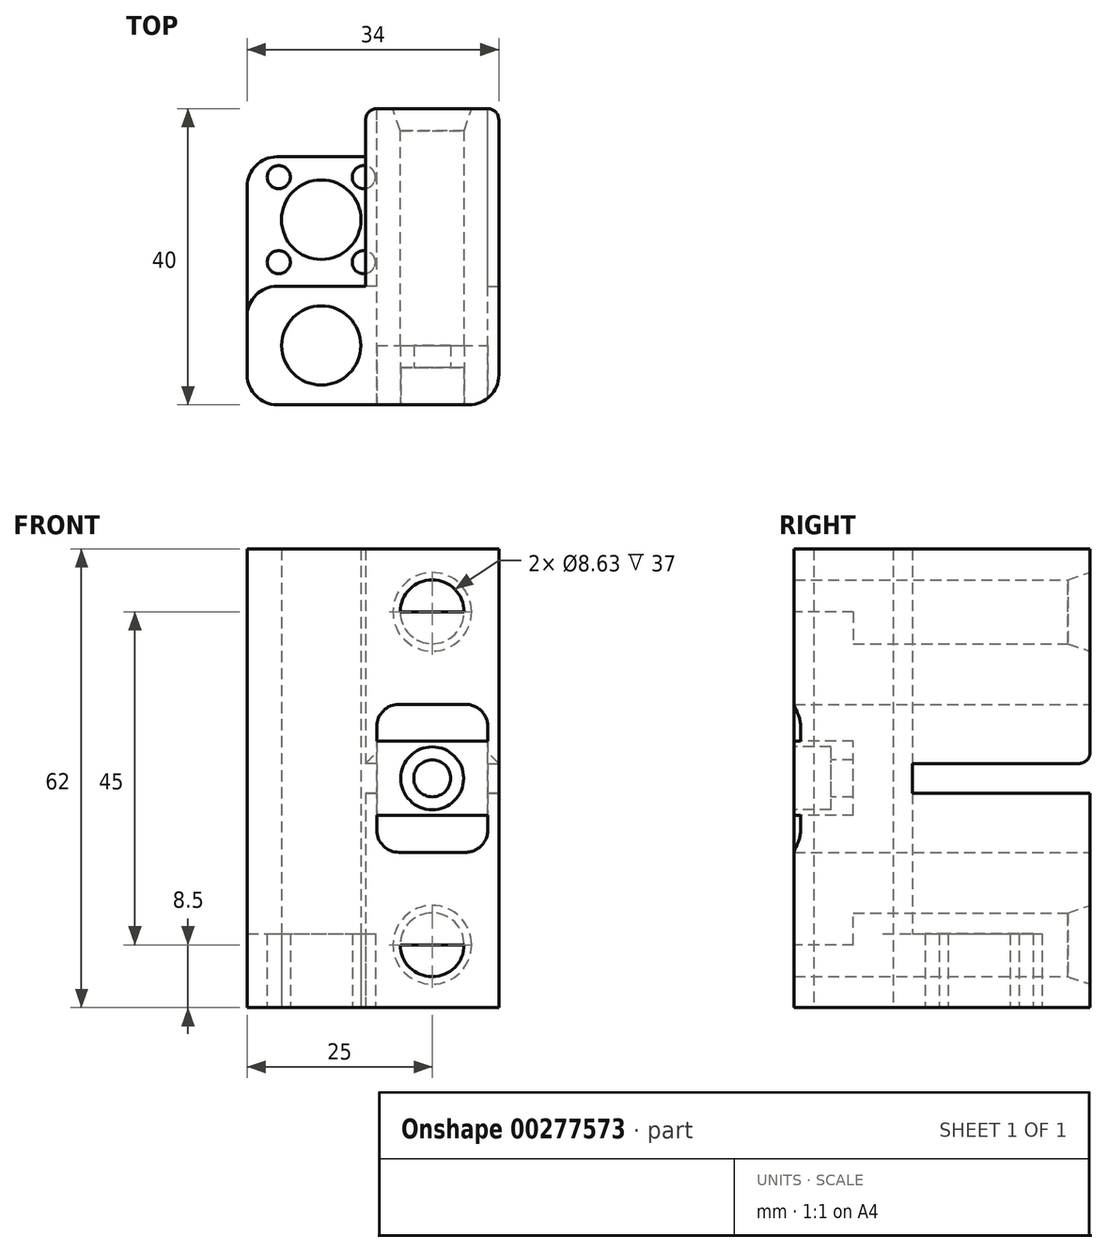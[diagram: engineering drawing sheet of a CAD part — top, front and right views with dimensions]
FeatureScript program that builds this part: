
annotation { "Feature Type Name" : "Feature", "Feature Type Description" : "" }
export const myFeature = defineFeature(function(context is Context, id is Id, definition is map)
    precondition{}
    {
        {
            var Q0;
            Q0=qCreatedBy(makeId("Front.planeOp"),FACE);
            var sketch = newSketch(context, id + "F0", { "sketchPlane" : qUnion([Q0])});
            skLineSegment(sketch, "E0.bottom", {"start": v(9, 31) * mm, "end": v(-9, 31) * mm});
            skLineSegment(sketch, "E0.top", {"start": v(9, -31) * mm, "end": v(-9, -31) * mm});
            skLineSegment(sketch, "E0.left", {"start": v(9, 31) * mm, "end": v(9, -31) * mm});
            skLineSegment(sketch, "E0.right", {"start": v(-9, 31) * mm, "end": v(-9, -31) * mm});
            skPoint(sketch, "E0.middle", {"position": v(0, 0) * mm});
            skCircle(sketch, "E1", {"center": v(0, 22.5) * mm, "radius": 4.32 * mm});
            skCircle(sketch, "E2", {"center": v(0, -22.5) * mm, "radius": 4.32 * mm});
            skLineSegment(sketch, "E3", {"start": v(0, 22.5) * mm, "end": v(0, 0) * mm, "construction": true});
            skLineSegment(sketch, "E4", {"start": v(0, 0) * mm, "end": v(0, -22.5) * mm, "construction": true});
            skSolve(sketch);
        }
        {
            var Q0;
            Q0=makeQuery(id+"F0.imprint","IMPRINT",FACE,{"disambiguationData":[TD([[makeQuery(id+"F0.imprint","IMPRINT",EDGE,{"derivedFrom":sQuery(id+"F0.wireOp",EDGE,"E0.bottom")}),1.0]])]});
            extrude(context, id + "F1", {"entities" : qUnion([Q0]), "depth" : 40 * mm, "offsetDistance" : 25 * mm});
        }
        {
            var Q0;
            Q0=makeQuery(id+"F1.opExtrude","SWEPT_FACE",FACE,{"disambiguationData":[OSD([sQuery(id+"F0.wireOp",EDGE,"E0.right")])]});
            var sketch = newSketch(context, id + "F2", { "sketchPlane" : qUnion([Q0])});
            skLineSegment(sketch, "E5", {"start": v(0, 0) * mm, "end": v(32, 0) * mm});
            skLineSegment(sketch, "E6.bottom", {"start": v(40, 31) * mm, "end": v(24, 31) * mm});
            skLineSegment(sketch, "E6.top", {"start": v(40, -31) * mm, "end": v(24, -31) * mm});
            skLineSegment(sketch, "E6.left", {"start": v(40, 31) * mm, "end": v(40, -31) * mm});
            skLineSegment(sketch, "E6.right", {"start": v(24, 31) * mm, "end": v(24, -31) * mm});
            skPoint(sketch, "E6.middle", {"position": v(32, 0) * mm});
            skSolve(sketch);
        }
        {
            var Q0;
            {var subQ1=sQuery(id+"F2.wireOp",EDGE,"E6.bottom");Q0=makeQuery(id+"F2.imprint","IMPRINT",FACE,{"disambiguationData":[TD([[makeQuery(id+"F2.imprint","IMPRINT",EDGE,{"derivedFrom":subQ1}),1.0]])]});}
            extrude(context, id + "F3", {"entities" : qUnion([Q0]), "operationType" : NewBodyOperationType.ADD, "depth" : 16 * mm, "offsetDistance" : 25 * mm});
        }
        {
            var Q0;
            Q0=makeQuery(id+"F3.boolean.opBoolean","MERGE",FACE,{"derivedFrom":[makeQuery(id+"F1.opExtrude","SWEPT_FACE",FACE,{"disambiguationData":[OSD([sQuery(id+"F0.wireOp",EDGE,"E0.top")])]}),makeQuery(id+"F3.opExtrude","SWEPT_FACE",FACE,{"disambiguationData":[OSD([sQuery(id+"F2.wireOp",EDGE,"E6.top")])]})]});
            var sketch = newSketch(context, id + "F4", { "sketchPlane" : qUnion([Q0])});
            skCircle(sketch, "E7", {"center": v(-15, 32) * mm, "radius": 5.35 * mm});
            skPoint(sketch, "E7.centerSnap0", {"position": v(-25, 32) * mm});
            skSolve(sketch);
        }
        {
            var Q0;
            Q0=makeQuery(id+"F4.imprint","IMPRINT",FACE,{"disambiguationData":[TD([[makeQuery(id+"F4.imprint","IMPRINT",EDGE,{"derivedFrom":sQuery(id+"F4.wireOp",EDGE,"E7")}),1.0]])]});
            extrude(context, id + "F5", {"entities" : qUnion([Q0]), "operationType" : NewBodyOperationType.REMOVE, "oppositeDirection" : true, "depth" : 100 * mm, "offsetDistance" : 25 * mm});
        }
        {
            var Q0;
            Q0=makeQuery(id+"F3.boolean.opBoolean","MERGE",FACE,{"derivedFrom":[makeQuery(id+"F1.opExtrude","SWEPT_FACE",FACE,{"disambiguationData":[OSD([sQuery(id+"F0.wireOp",EDGE,"E0.top")])]}),makeQuery(id+"F3.opExtrude","SWEPT_FACE",FACE,{"disambiguationData":[OSD([sQuery(id+"F2.wireOp",EDGE,"E6.top")])]})]});
            var sketch = newSketch(context, id + "F6", { "sketchPlane" : qUnion([Q0])});
            skLineSegment(sketch, "E8", {"start": v(-15, 32) * mm, "end": v(-15, 0.7) * mm, "construction": true});
            skCircle(sketch, "E9", {"center": v(-15, 15) * mm, "radius": 5.38 * mm});
            skLineSegment(sketch, "E10.bottom", {"start": v(-9, 24) * mm, "end": v(-25, 24) * mm});
            skLineSegment(sketch, "E10.top", {"start": v(-9, 6.5) * mm, "end": v(-25, 6.5) * mm});
            skLineSegment(sketch, "E10.left", {"start": v(-9, 24) * mm, "end": v(-9, 6.5) * mm});
            skLineSegment(sketch, "E10.right", {"start": v(-25, 24) * mm, "end": v(-25, 6.5) * mm});
            skLineSegment(sketch, "E11.bottom", {"start": v(-9.25, 20.75) * mm, "end": v(-20.75, 20.75) * mm, "construction": true});
            skLineSegment(sketch, "E11.top", {"start": v(-9.25, 9.25) * mm, "end": v(-20.75, 9.25) * mm, "construction": true});
            skLineSegment(sketch, "E11.left", {"start": v(-9.25, 20.75) * mm, "end": v(-9.25, 9.25) * mm, "construction": true});
            skLineSegment(sketch, "E11.right", {"start": v(-20.75, 20.75) * mm, "end": v(-20.75, 9.25) * mm, "construction": true});
            skCircle(sketch, "E12", {"center": v(-20.75, 20.75) * mm, "radius": 1.56 * mm});
            skCircle(sketch, "E13", {"center": v(-9.25, 20.75) * mm, "radius": 1.56 * mm});
            skCircle(sketch, "E14", {"center": v(-9.25, 9.25) * mm, "radius": 1.56 * mm});
            skCircle(sketch, "E15", {"center": v(-20.75, 9.25) * mm, "radius": 1.56 * mm});
            skSolve(sketch);
        }
        {
            var Q0;
            Q0=makeQuery(id+"F6.imprint","IMPRINT",FACE,{"disambiguationData":[TD([[makeQuery(id+"F6.imprint","IMPRINT",EDGE,{"derivedFrom":sQuery(id+"F6.wireOp",EDGE,"E9")}),-1.0]])]});
            extrude(context, id + "F7", {"entities" : qUnion([Q0]), "operationType" : NewBodyOperationType.ADD, "oppositeDirection" : true, "depth" : 10 * mm, "offsetDistance" : 25 * mm});
        }
        {
            var Q0;
            {var subQ0=sQuery(id+"F6.wireOp",EDGE,"E13");var subQ1=sQuery(id+"F6.wireOp",EDGE,"E10.left");var subQ2=makeQuery(id+"F6.imprint","INTERSECT",VERTEX,{"disambiguationData":[OD(0.0)],"derivedFrom":[subQ1,subQ0]});Q0=makeQuery(id+"F6.imprint","IMPRINT",FACE,{"disambiguationData":[TD([[makeQuery(id+"F6.imprint","IMPRINT",EDGE,{"disambiguationData":[TD([[subQ2,-1.0]])],"derivedFrom":subQ1}),1.0]])]});}
            var Q1;
            {var subQ0=sQuery(id+"F6.wireOp",EDGE,"E14");var subQ1=sQuery(id+"F6.wireOp",EDGE,"E10.left");var subQ2=makeQuery(id+"F6.imprint","INTERSECT",VERTEX,{"disambiguationData":[OD(0.0)],"derivedFrom":[subQ1,subQ0]});Q1=makeQuery(id+"F6.imprint","IMPRINT",FACE,{"disambiguationData":[TD([[makeQuery(id+"F6.imprint","IMPRINT",EDGE,{"disambiguationData":[TD([[subQ2,-1.0]])],"derivedFrom":subQ1}),1.0]])]});}
            extrude(context, id + "F8", {"entities" : qUnion([Q0, Q1]), "operationType" : NewBodyOperationType.REMOVE, "oppositeDirection" : true, "depth" : 10 * mm, "offsetDistance" : 25 * mm});
        }
        {
            var Q0;
            Q0=makeQuery(id+"F1.opExtrude","CAP_FACE",FACE,{"disambiguationData":[OSD([sQuery(id+"F0.wireOp",EDGE,"E0.bottom"),sQuery(id+"F0.wireOp",EDGE,"E0.top"),sQuery(id+"F0.wireOp",EDGE,"E0.left"),sQuery(id+"F0.wireOp",EDGE,"E0.right"),sQuery(id+"F0.wireOp",EDGE,"E1"),sQuery(id+"F0.wireOp",EDGE,"E2")])],"isStart":true});
            var sketch = newSketch(context, id + "F9", { "sketchPlane" : qUnion([Q0])});
            skLineSegment(sketch, "E16.bottom", {"start": v(7.5, 10) * mm, "end": v(-7.5, 10) * mm});
            skLineSegment(sketch, "E16.top", {"start": v(7.5, -10) * mm, "end": v(-7.5, -10) * mm});
            skLineSegment(sketch, "E16.left", {"start": v(7.5, 10) * mm, "end": v(7.5, -10) * mm});
            skLineSegment(sketch, "E16.right", {"start": v(-7.5, 10) * mm, "end": v(-7.5, -10) * mm});
            skPoint(sketch, "E16.middle", {"position": v(0, 0) * mm});
            skLineSegment(sketch, "E17", {"start": v(0, 0) * mm, "end": v(-13.25, 0) * mm});
            skPoint(sketch, "E17.endSnap0", {"position": v(-9, 0) * mm});
            skLineSegment(sketch, "E18", {"start": v(0, 0) * mm, "end": v(13.25, 0) * mm});
            skPoint(sketch, "E18.endSnap0", {"position": v(9, 0) * mm});
            skLineSegment(sketch, "E19.bottom", {"start": v(-7.5, 2) * mm, "end": v(-19, 2) * mm});
            skLineSegment(sketch, "E19.top", {"start": v(-7.5, -2) * mm, "end": v(-19, -2) * mm});
            skLineSegment(sketch, "E19.left", {"start": v(-7.5, 2) * mm, "end": v(-7.5, -2) * mm});
            skLineSegment(sketch, "E19.right", {"start": v(-19, 2) * mm, "end": v(-19, -2) * mm});
            skPoint(sketch, "E19.middle", {"position": v(-13.25, 0) * mm});
            skLineSegment(sketch, "E20.bottom", {"start": v(7.5, 2) * mm, "end": v(19, 2) * mm});
            skLineSegment(sketch, "E20.top", {"start": v(7.5, -2) * mm, "end": v(19, -2) * mm});
            skLineSegment(sketch, "E20.left", {"start": v(7.5, 2) * mm, "end": v(7.5, -2) * mm});
            skLineSegment(sketch, "E20.right", {"start": v(19, 2) * mm, "end": v(19, -2) * mm});
            skPoint(sketch, "E20.middle", {"position": v(13.25, 0) * mm});
            skSolve(sketch);
        }
        {
            var Q0;
            {var subQ1=sQuery(id+"F9.wireOp",EDGE,"E16.bottom");Q0=makeQuery(id+"F9.imprint","IMPRINT",FACE,{"disambiguationData":[TD([[makeQuery(id+"F9.imprint","IMPRINT",EDGE,{"derivedFrom":subQ1}),1.0]])]});}
            var Q1;
            {var subQ1=sQuery(id+"F9.wireOp",EDGE,"E16.top");Q1=makeQuery(id+"F9.imprint","IMPRINT",FACE,{"disambiguationData":[TD([[makeQuery(id+"F9.imprint","IMPRINT",EDGE,{"derivedFrom":subQ1}),-1.0]])]});}
            extrude(context, id + "F10", {"entities" : qUnion([Q0, Q1]), "operationType" : NewBodyOperationType.REMOVE, "oppositeDirection" : true, "depth" : 100 * mm, "offsetDistance" : 25 * mm});
        }
        {
            var Q0;
            {var subQ0=sQuery(id+"F9.wireOp",EDGE,"E17");var subQ1=sQuery(id+"F9.wireOp",EDGE,"E16.right");var subQ2=makeQuery(id+"F9.imprint","INTERSECT",VERTEX,{"derivedFrom":[subQ1,subQ0]});Q0=makeQuery(id+"F9.imprint","IMPRINT",FACE,{"disambiguationData":[TD([[makeQuery(id+"F9.imprint","IMPRINT",EDGE,{"disambiguationData":[TD([[subQ2,-1.0]])],"derivedFrom":subQ1}),-1.0]])]});}
            var Q1;
            {var subQ0=sQuery(id+"F9.wireOp",EDGE,"E17");var subQ1=sQuery(id+"F9.wireOp",EDGE,"E16.right");var subQ2=makeQuery(id+"F9.imprint","INTERSECT",VERTEX,{"derivedFrom":[subQ1,subQ0]});Q1=makeQuery(id+"F9.imprint","IMPRINT",FACE,{"disambiguationData":[TD([[makeQuery(id+"F9.imprint","IMPRINT",EDGE,{"disambiguationData":[TD([[subQ2,1.0]])],"derivedFrom":subQ1}),-1.0]])]});}
            var Q2;
            {var subQ0=sQuery(id+"F9.wireOp",EDGE,"E18");var subQ1=sQuery(id+"F9.wireOp",EDGE,"E16.left");var subQ2=makeQuery(id+"F9.imprint","INTERSECT",VERTEX,{"derivedFrom":[subQ1,subQ0]});Q2=makeQuery(id+"F9.imprint","IMPRINT",FACE,{"disambiguationData":[TD([[makeQuery(id+"F9.imprint","IMPRINT",EDGE,{"disambiguationData":[TD([[subQ2,-1.0]])],"derivedFrom":subQ1}),1.0]])]});}
            var Q3;
            {var subQ0=sQuery(id+"F9.wireOp",EDGE,"E18");var subQ1=sQuery(id+"F9.wireOp",EDGE,"E16.left");var subQ2=makeQuery(id+"F9.imprint","INTERSECT",VERTEX,{"derivedFrom":[subQ1,subQ0]});Q3=makeQuery(id+"F9.imprint","IMPRINT",FACE,{"disambiguationData":[TD([[makeQuery(id+"F9.imprint","IMPRINT",EDGE,{"disambiguationData":[TD([[subQ2,1.0]])],"derivedFrom":subQ1}),1.0]])]});}
            extrude(context, id + "F11", {"entities" : qUnion([Q0, Q1, Q2, Q3]), "operationType" : NewBodyOperationType.REMOVE, "oppositeDirection" : true, "depth" : 24 * mm, "offsetDistance" : 25 * mm});
        }
        {
            var Q0;
            Q0=makeQuery(id+"F3.boolean.opBoolean","MERGE",FACE,{"derivedFrom":[makeQuery(id+"F1.opExtrude","CAP_FACE",FACE,{"disambiguationData":[OSD([sQuery(id+"F0.wireOp",EDGE,"E0.bottom"),sQuery(id+"F0.wireOp",EDGE,"E0.top"),sQuery(id+"F0.wireOp",EDGE,"E0.left"),sQuery(id+"F0.wireOp",EDGE,"E0.right"),sQuery(id+"F0.wireOp",EDGE,"E1"),sQuery(id+"F0.wireOp",EDGE,"E2")])],"isStart":false}),makeQuery(id+"F3.opExtrude","SWEPT_FACE",FACE,{"disambiguationData":[OSD([sQuery(id+"F2.wireOp",EDGE,"E6.left")])]})]});
            var sketch = newSketch(context, id + "F12", { "sketchPlane" : qUnion([Q0])});
            skLineSegment(sketch, "E21.bottom", {"start": v(-7.5, 5) * mm, "end": v(7.5, 5) * mm});
            skLineSegment(sketch, "E21.top", {"start": v(-7.5, -5) * mm, "end": v(7.5, -5) * mm});
            skLineSegment(sketch, "E21.left", {"start": v(-7.5, 5) * mm, "end": v(-7.5, -5) * mm});
            skLineSegment(sketch, "E21.right", {"start": v(7.5, 5) * mm, "end": v(7.5, -5) * mm});
            skLineSegment(sketch, "E22", {"start": v(0, 22.5) * mm, "end": v(4.32, 22.5) * mm});
            skLineSegment(sketch, "E23", {"start": v(0, 22.5) * mm, "end": v(-4.32, 22.5) * mm});
            skLineSegment(sketch, "E24", {"start": v(0, -22.5) * mm, "end": v(4.32, -22.5) * mm});
            skLineSegment(sketch, "E25", {"start": v(0, -22.5) * mm, "end": v(-4.32, -22.5) * mm});
            skPoint(sketch, "E26", {"position": v(0, 0) * mm});
            skSolve(sketch);
        }
        {
            var Q0;
            Q0=makeQuery(id+"F12.imprint","IMPRINT",FACE,{"disambiguationData":[TD([[makeQuery(id+"F12.imprint","IMPRINT",EDGE,{"derivedFrom":sQuery(id+"F12.wireOp",EDGE,"E21.bottom")}),-1.0]])]});
            var Q1;
            {var subQ0=sQuery(id+"F12.wireOp",EDGE,"E22");Q1=makeQuery(id+"F12.imprint","IMPRINT",FACE,{"disambiguationData":[TD([[makeQuery(id+"F12.imprint","IMPRINT",EDGE,{"derivedFrom":subQ0}),-1.0]])]});}
            var Q2;
            {var subQ0=sQuery(id+"F12.wireOp",EDGE,"E24");Q2=makeQuery(id+"F12.imprint","IMPRINT",FACE,{"disambiguationData":[TD([[makeQuery(id+"F12.imprint","IMPRINT",EDGE,{"derivedFrom":subQ0}),1.0]])]});}
            extrude(context, id + "F13", {"entities" : qUnion([Q0, Q1, Q2]), "operationType" : NewBodyOperationType.ADD, "oppositeDirection" : true, "depth" : 8 * mm, "offsetDistance" : 25 * mm});
        }
        {
            var Q0;
            Q0=makeQuery(id+"F1.opExtrude","CAP_EDGE",EDGE,{"disambiguationData":[OSD([sQuery(id+"F0.wireOp",EDGE,"E1")])],"isStart":true});
            var Q1;
            Q1=makeQuery(id+"F1.opExtrude","CAP_EDGE",EDGE,{"disambiguationData":[OSD([sQuery(id+"F0.wireOp",EDGE,"E2")])],"isStart":true});
            chamfer(context, id + "F14", {"entities" : qUnion([Q0, Q1]), "chamferType" : ChamferType.TWO_OFFSETS, "width1" : 1 * mm, "oppositeDirection" : false, "width2" : 3 * mm, "tangentPropagation" : true});
        }
        {
            var Q0;
            Q0=makeQuery(id+"F10.boolean.opBoolean","COPY",EDGE,{"derivedFrom":makeQuery(id+"F10.opExtrude","SWEPT_EDGE",EDGE,{"disambiguationData":[OSD([sQuery(id+"F9.wireOp",EDGE,"E16.bottom"),sQuery(id+"F9.wireOp",EDGE,"E16.left")])]})});
            var Q1;
            Q1=makeQuery(id+"F10.boolean.opBoolean","COPY",EDGE,{"derivedFrom":makeQuery(id+"F10.opExtrude","SWEPT_EDGE",EDGE,{"disambiguationData":[OSD([sQuery(id+"F9.wireOp",EDGE,"E16.bottom"),sQuery(id+"F9.wireOp",EDGE,"E16.right")])]})});
            var Q2;
            Q2=makeQuery(id+"F10.boolean.opBoolean","COPY",EDGE,{"derivedFrom":makeQuery(id+"F10.opExtrude","SWEPT_EDGE",EDGE,{"disambiguationData":[OSD([sQuery(id+"F9.wireOp",EDGE,"E16.top"),sQuery(id+"F9.wireOp",EDGE,"E16.right")])]})});
            var Q3;
            Q3=makeQuery(id+"F10.boolean.opBoolean","COPY",EDGE,{"derivedFrom":makeQuery(id+"F10.opExtrude","SWEPT_EDGE",EDGE,{"disambiguationData":[OSD([sQuery(id+"F9.wireOp",EDGE,"E16.top"),sQuery(id+"F9.wireOp",EDGE,"E16.left")])]})});
            fillet(context, id + "F15", {"entities" : qUnion([Q0, Q1, Q2, Q3]), "tangentPropagation" : true, "radius" : 3 * mm, "defaultsChanged" : false, "vertexSettings" : [], "allowEdgeOverflow" : false});
        }
        {
            var Q0;
            Q0=makeQuery(id+"F3.opExtrude","CAP_EDGE",EDGE,{"disambiguationData":[OSD([sQuery(id+"F2.wireOp",EDGE,"E6.right")])],"isStart":false});
            var Q1;
            Q1=makeQuery(id+"F3.opExtrude","CAP_EDGE",EDGE,{"disambiguationData":[OSD([sQuery(id+"F2.wireOp",EDGE,"E6.left")])],"isStart":false});
            var Q2;
            Q2=makeQuery(id+"F1.opExtrude","CAP_EDGE",EDGE,{"disambiguationData":[OSD([sQuery(id+"F0.wireOp",EDGE,"E0.left")])],"isStart":false});
            var Q3;
            Q3=makeQuery(id+"F7.opExtrude","SWEPT_EDGE",EDGE,{"disambiguationData":[OSD([sQuery(id+"F6.wireOp",EDGE,"E10.top"),sQuery(id+"F6.wireOp",EDGE,"E10.right")])]});
            fillet(context, id + "F16", {"entities" : qUnion([Q0, Q1, Q2, Q3]), "tangentPropagation" : true, "radius" : 4 * mm, "defaultsChanged" : true, "vertexSettings" : [], "allowEdgeOverflow" : false});
        }
        {
            var Q0;
            Q0=makeQuery(id+"F7.opExtrude","SWEPT_EDGE",EDGE,{"disambiguationData":[OSD([sQuery(id+"F6.wireOp",EDGE,"E10.top"),sQuery(id+"F6.wireOp",EDGE,"E10.right")])]});
            var Q1;
            {var subQ0=sQuery(id+"F0.wireOp",EDGE,"E0.right");var subQ1=sQuery(id+"F0.wireOp",EDGE,"E0.top");Q1=makeQuery(id+"F11.boolean.opBoolean","SPLIT",EDGE,{"disambiguationData":[TD([makeQuery(id+"F1.opExtrude","SWEPT_FACE",FACE,{"disambiguationData":[OSD([subQ1])]})])],"derivedFrom":makeQuery(id+"F1.opExtrude","CAP_EDGE",EDGE,{"disambiguationData":[OSD([subQ0])],"isStart":true})});}
            var Q2;
            {var subQ0=sQuery(id+"F0.wireOp",EDGE,"E0.left");var subQ1=sQuery(id+"F0.wireOp",EDGE,"E0.top");Q2=makeQuery(id+"F11.boolean.opBoolean","SPLIT",EDGE,{"disambiguationData":[TD([makeQuery(id+"F1.opExtrude","SWEPT_FACE",FACE,{"disambiguationData":[OSD([subQ1])]})])],"derivedFrom":makeQuery(id+"F1.opExtrude","CAP_EDGE",EDGE,{"disambiguationData":[OSD([subQ0])],"isStart":true})});}
            var Q3;
            {var subQ0=sQuery(id+"F9.wireOp",EDGE,"E20.top");var subQ2=sQuery(id+"F2.wireOp",EDGE,"E6.right");Q3=makeQuery(id+"F11.boolean.opBoolean","SPLIT",EDGE,{"disambiguationData":[TD([makeQuery(id+"F11.opExtrude","SWEPT_FACE",FACE,{"disambiguationData":[OSD([subQ0])]})])],"derivedFrom":makeQuery(id+"F3.opExtrude","CAP_EDGE",EDGE,{"disambiguationData":[OSD([subQ2])],"isStart":true})});}
            var Q4;
            {var subQ0=sQuery(id+"F2.wireOp",EDGE,"E6.right");Q4=makeQuery(id+"F11.boolean.opBoolean","SPLIT",EDGE,{"disambiguationData":[TD([makeQuery(id+"F1.opExtrude","SWEPT_FACE",FACE,{"disambiguationData":[OSD([sQuery(id+"F0.wireOp",EDGE,"E0.bottom")])]})])],"derivedFrom":makeQuery(id+"F3.opExtrude","CAP_EDGE",EDGE,{"disambiguationData":[OSD([subQ0])],"isStart":true})});}
            var Q5;
            {var subQ0=sQuery(id+"F0.wireOp",EDGE,"E0.left");var subQ1=sQuery(id+"F0.wireOp",EDGE,"E0.bottom");Q5=makeQuery(id+"F11.boolean.opBoolean","SPLIT",EDGE,{"disambiguationData":[TD([makeQuery(id+"F1.opExtrude","SWEPT_FACE",FACE,{"disambiguationData":[OSD([subQ1])]})])],"derivedFrom":makeQuery(id+"F1.opExtrude","CAP_EDGE",EDGE,{"disambiguationData":[OSD([subQ0])],"isStart":true})});}
            var Q6;
            {var subQ0=sQuery(id+"F0.wireOp",EDGE,"E0.right");var subQ1=sQuery(id+"F0.wireOp",EDGE,"E0.bottom");Q6=makeQuery(id+"F11.boolean.opBoolean","SPLIT",EDGE,{"disambiguationData":[TD([makeQuery(id+"F1.opExtrude","SWEPT_FACE",FACE,{"disambiguationData":[OSD([subQ1])]})])],"derivedFrom":makeQuery(id+"F1.opExtrude","CAP_EDGE",EDGE,{"disambiguationData":[OSD([subQ0])],"isStart":true})});}
            var Q7;
            Q7=makeQuery(id+"F11.boolean.opBoolean","COPY",EDGE,{"derivedFrom":makeQuery(id+"F11.opExtrude","CAP_EDGE",EDGE,{"disambiguationData":[OSD([sQuery(id+"F9.wireOp",EDGE,"E20.bottom")])],"isStart":true})});
            var Q8;
            Q8=makeQuery(id+"F11.boolean.opBoolean","COPY",EDGE,{"derivedFrom":makeQuery(id+"F11.opExtrude","CAP_EDGE",EDGE,{"disambiguationData":[OSD([sQuery(id+"F9.wireOp",EDGE,"E20.top")])],"isStart":true})});
            var Q9;
            Q9=makeQuery(id+"F11.boolean.opBoolean","COPY",EDGE,{"derivedFrom":makeQuery(id+"F11.opExtrude","CAP_EDGE",EDGE,{"disambiguationData":[OSD([sQuery(id+"F9.wireOp",EDGE,"E19.top")])],"isStart":true})});
            var Q10;
            Q10=makeQuery(id+"F11.boolean.opBoolean","COPY",EDGE,{"derivedFrom":makeQuery(id+"F11.opExtrude","CAP_EDGE",EDGE,{"disambiguationData":[OSD([sQuery(id+"F9.wireOp",EDGE,"E19.bottom")])],"isStart":true})});
            fillet(context, id + "F17", {"entities" : qUnion([Q0, Q1, Q2, Q3, Q4, Q5, Q6, Q7, Q8, Q9, Q10]), "tangentPropagation" : true, "radius" : 1.5 * mm, "defaultsChanged" : true, "vertexSettings" : [], "allowEdgeOverflow" : false});
        }
        {
            var Q0;
            Q0=sQuery(id+"F12.wireOp",VERTEX,"E26");
            var Q1;
            Q1=makeQuery(id+"F1.opExtrude","SWEPT_BODY",BODY,{"disambiguationData":[OSD([sQuery(id+"F0.wireOp",EDGE,"E0.bottom"),sQuery(id+"F0.wireOp",EDGE,"E0.top"),sQuery(id+"F0.wireOp",EDGE,"E0.left"),sQuery(id+"F0.wireOp",EDGE,"E0.right"),sQuery(id+"F0.wireOp",EDGE,"E1"),sQuery(id+"F0.wireOp",EDGE,"E2")])]});
            hole(context, id + "F18", {"style" : HoleStyle.C_BORE, "endStyle" : HoleEndStyle.BLIND, "holeDiameter" : 5 * mm, "cBoreDiameter" : 8.5 * mm, "cBoreDepth" : 5 * mm, "majorDiameter" : 5 * mm, "holeDepth" : 10 * mm, "tappedDepth" : 12 * mm, "tapClearance" : 3, "locations" : qUnion([Q0]), "scope" : qUnion([Q1])});
        }
    });
